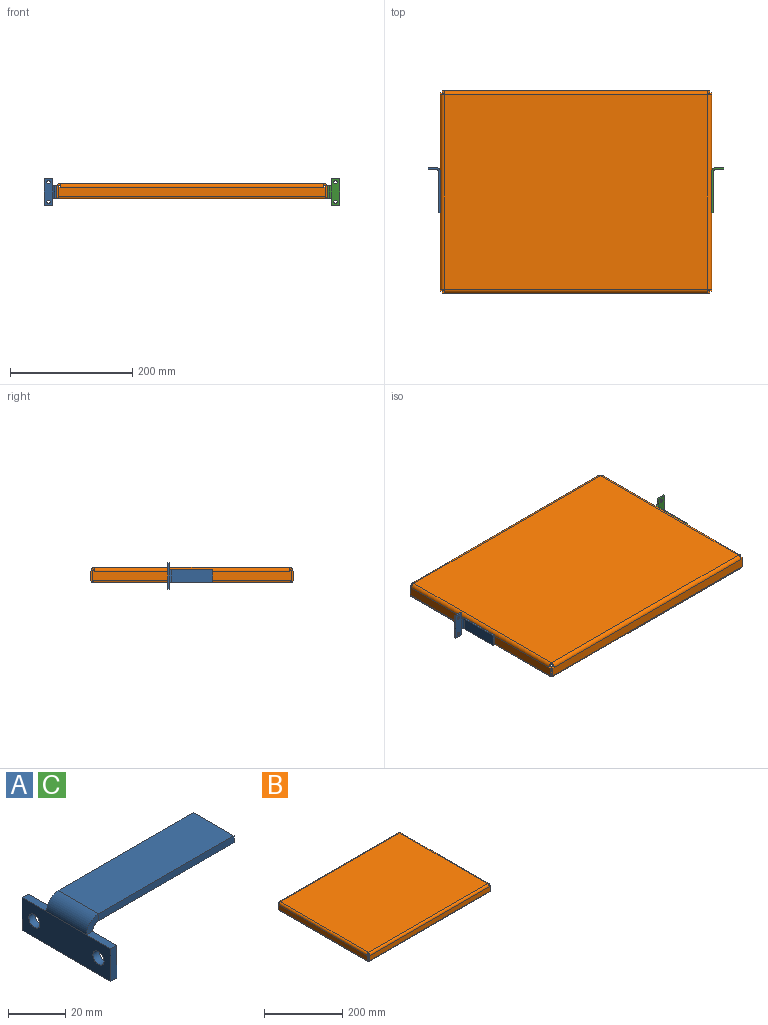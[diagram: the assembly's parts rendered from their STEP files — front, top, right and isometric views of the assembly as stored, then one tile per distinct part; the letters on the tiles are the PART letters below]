
ASSEMBLY  parts=3 mates=6
PART A: 18 faces, bbox 73x44x20 mm
  f0: plane 67x3mm, normal (0,1,0), area 201mm2, adj f2,f3,f4,f15
  f1: plane 67x3mm, normal (0,-1,0), area 201mm2, adj f2,f3,f4,f14
  f2: plane 20x3mm, normal (1,0,0), area 60mm2, adj f0,f1,f3,f4
  f3: plane 67x20mm, normal (0,0,1), area 1340mm2, adj f0,f1,f2,f16
  f4: plane 67x20mm, normal (0,0,-1), area 1340mm2, adj f0,f1,f2,f17
  f5: plane 12x3mm, normal (0,0,1), area 36mm2, adj f6,f12,f13,f15
  f6: plane 14x3mm, normal (0,1,0), area 42mm2, adj f5,f7,f12,f13
  f7: plane 44x3mm, normal (0,0,-1), area 132mm2, adj f6,f8,f12,f13
  f8: plane 14x3mm, normal (0,-1,0), area 42mm2, adj f7,f9,f12,f13
  f9: plane 12x3mm, normal (0,0,1), area 36mm2, adj f8,f12,f13,f14
  f10: cylinder r=2.75mm len=5.5mm, axis (-1,0,0), area 51.8mm2, adj f12,f13
  f11: cylinder r=2.75mm len=5.5mm, axis (-1,0,0), area 51.8mm2, adj f12,f13
  f12: plane 44x14mm, normal (-1,0,0), area 568.5mm2, adj f5,f6,f7,f8,f9,f10,f11,f16
  f13: plane 44x14mm, normal (1,0,0), area 568.5mm2, adj f5,f6,f7,f8,f9,f10,f11,f17
  f14: plane 6x6mm, normal (0,-1,0), area 21.2mm2, adj f1,f9,f16,f17
  f15: plane 6x6mm, normal (0,1,0), area 21.2mm2, adj f0,f5,f16,f17
  f16: cylinder r=6mm len=20mm, axis (0,-1,0), area 188.5mm2, adj f3,f12,f14,f15
  f17: cylinder r=3mm len=20mm, axis (0,-1,0), area 94.2mm2, adj f4,f13,f14,f15
PART B: 78 faces, bbox 443x330x25 mm
  f0: plane 431x318mm, normal (0,0,1), area 137058mm2, adj f19,f29,f57,f67
  f1: plane 431x318mm, normal (0,0,-1), area 137058mm2, adj f20,f30,f58,f68
  f2: plane 3x2.98mm, normal (0,0,1), area 8.9mm2, adj f3,f6,f7,f18
  f3: plane 15.99x3mm, normal (1,0,0), area 48mm2, adj f2,f6,f7,f9
  f4: plane 3x2.98mm, normal (0,0,1), area 8.9mm2, adj f5,f6,f7,f17
  f5: plane 15.99x3mm, normal (-1,0,0), area 48mm2, adj f4,f6,f7,f8
  f6: plane 436.96x15.99mm, normal (0,-1,0), area 6987mm2, adj f2,f3,f4,f5,f10,f19
  f7: plane 436.96x15.99mm, normal (0,1,0), area 6987mm2, adj f2,f3,f4,f5,f11,f20
  f8: bspline ~6.02x3.19mm, area 17.9mm2, adj f5,f10,f11,f12
  f9: bspline ~6.02x3.19mm, area 17.9mm2, adj f3,f10,f11,f14
  f10: cylinder r=3.01mm len=436.96mm, axis (1,0,0), area 4101.8mm2, adj f6,f8,f9,f15
  f11: cylinder r=0.01mm len=436.96mm, axis (1,0,0), area 13.6mm2, adj f7,f8,f9,f16
  f12: plane 14.99x3mm, normal (-1,0,0), area 45mm2, adj f8,f13,f15,f16
  f13: plane 430.59x3mm, normal (0,0,1), area 1291.8mm2, adj f12,f14,f15,f16
  f14: plane 14.99x3mm, normal (1,0,0), area 45mm2, adj f9,f13,f15,f16
  f15: plane 430.59x14.99mm, normal (0,1,0), area 6454.5mm2, adj f10,f12,f13,f14
  f16: plane 430.59x14.99mm, normal (0,-1,0), area 6454.5mm2, adj f11,f12,f13,f14
  f17: plane 6x6mm, normal (-1,0,0), area 21.2mm2, adj f4,f19,f20,f66
  f18: plane 6x6mm, normal (1,0,0), area 21.2mm2, adj f2,f19,f20,f56
  f19: cylinder r=6mm len=431mm, axis (-1,0,0), area 4062.1mm2, adj f0,f6,f17,f18
  f20: cylinder r=3mm len=431mm, axis (-1,0,0), area 2031mm2, adj f1,f7,f17,f18
  f21: plane 3x2.98mm, normal (0,0,1), area 8.9mm2, adj f22,f25,f26,f27
  f22: plane 15.99x3mm, normal (-1,0,0), area 48mm2, adj f21,f25,f26,f32
  f23: plane 3x2.98mm, normal (0,0,1), area 8.9mm2, adj f24,f25,f26,f28
  f24: plane 15.99x3mm, normal (1,0,0), area 48mm2, adj f23,f25,f26,f31
  f25: plane 436.96x15.99mm, normal (0,1,0), area 6987mm2, adj f21,f22,f23,f24,f29,f33
  f26: plane 436.96x15.99mm, normal (0,-1,0), area 6987mm2, adj f21,f22,f23,f24,f30,f34
  f27: plane 6x6mm, normal (-1,0,0), area 21.2mm2, adj f21,f29,f30,f65
  f28: plane 6x6mm, normal (1,0,0), area 21.2mm2, adj f23,f29,f30,f55
  f29: cylinder r=6mm len=431mm, axis (-1,0,0), area 4062.1mm2, adj f0,f25,f27,f28
  f30: cylinder r=3mm len=431mm, axis (-1,0,0), area 2031mm2, adj f1,f26,f27,f28
  f31: bspline ~6.02x3.19mm, area 17.9mm2, adj f24,f33,f34,f35
  f32: bspline ~6.02x3.19mm, area 17.9mm2, adj f22,f33,f34,f37
  f33: cylinder r=3.01mm len=436.96mm, axis (-1,0,0), area 4101.8mm2, adj f25,f31,f32,f38
  f34: cylinder r=0.01mm len=436.96mm, axis (-1,0,0), area 13.6mm2, adj f26,f31,f32,f39
  f35: plane 14.99x3mm, normal (1,0,0), area 45mm2, adj f31,f36,f38,f39
  f36: plane 430.59x3mm, normal (0,0,1), area 1291.8mm2, adj f35,f37,f38,f39
  f37: plane 14.99x3mm, normal (-1,0,0), area 45mm2, adj f32,f36,f38,f39
  f38: plane 430.59x14.99mm, normal (0,-1,0), area 6454.5mm2, adj f33,f35,f36,f37
  f39: plane 430.59x14.99mm, normal (0,1,0), area 6454.5mm2, adj f34,f35,f36,f37
  f40: plane 3x2.98mm, normal (0,0,1), area 8.9mm2, adj f41,f44,f45,f55
  f41: plane 15.99x3mm, normal (0,1,0), area 48mm2, adj f40,f44,f45,f47
  f42: plane 3x2.98mm, normal (0,0,1), area 8.9mm2, adj f43,f44,f45,f56
  f43: plane 15.99x3mm, normal (0,-1,0), area 48mm2, adj f42,f44,f45,f46
  f44: plane 323.96x15.99mm, normal (1,0,0), area 5180.1mm2, adj f40,f41,f42,f43,f48,f57
  f45: plane 323.96x15.99mm, normal (-1,0,0), area 5180.1mm2, adj f40,f41,f42,f43,f49,f58
  f46: bspline ~6.02x3.19mm, area 17.9mm2, adj f43,f48,f49,f50
  f47: bspline ~6.02x3.19mm, area 17.9mm2, adj f41,f48,f49,f52
  f48: cylinder r=3.01mm len=323.96mm, axis (0,1,0), area 3033.3mm2, adj f44,f46,f47,f53
  f49: cylinder r=0.01mm len=323.96mm, axis (0,1,0), area 10.1mm2, adj f45,f46,f47,f54
  f50: plane 14.99x3mm, normal (0,-1,0), area 45mm2, adj f46,f51,f53,f54
  f51: plane 317.59x3mm, normal (0,0,1), area 952.8mm2, adj f50,f52,f53,f54
  f52: plane 14.99x3mm, normal (0,1,0), area 45mm2, adj f47,f51,f53,f54
  f53: plane 317.59x14.99mm, normal (-1,0,0), area 4760.6mm2, adj f48,f50,f51,f52
  f54: plane 317.59x14.99mm, normal (1,0,0), area 4760.6mm2, adj f49,f50,f51,f52
  f55: plane 6x6mm, normal (0,1,0), area 21.2mm2, adj f28,f40,f57,f58
  f56: plane 6x6mm, normal (0,-1,0), area 21.2mm2, adj f18,f42,f57,f58
  f57: cylinder r=6mm len=318mm, axis (0,1,0), area 2997.1mm2, adj f0,f44,f55,f56
  f58: cylinder r=3mm len=318mm, axis (0,1,0), area 1498.5mm2, adj f1,f45,f55,f56
  f59: plane 3x2.98mm, normal (0,0,1), area 8.9mm2, adj f60,f63,f64,f66
  f60: plane 15.99x3mm, normal (0,-1,0), area 48mm2, adj f59,f63,f64,f70
  f61: plane 3x2.98mm, normal (0,0,1), area 8.9mm2, adj f62,f63,f64,f65
  f62: plane 15.99x3mm, normal (0,1,0), area 48mm2, adj f61,f63,f64,f69
  f63: plane 323.96x15.99mm, normal (-1,0,0), area 5180.1mm2, adj f59,f60,f61,f62,f67,f71
  f64: plane 323.96x15.99mm, normal (1,0,0), area 5180.1mm2, adj f59,f60,f61,f62,f68,f72
  f65: plane 6x6mm, normal (0,1,0), area 21.2mm2, adj f27,f61,f67,f68
  f66: plane 6x6mm, normal (0,-1,0), area 21.2mm2, adj f17,f59,f67,f68
  f67: cylinder r=6mm len=318mm, axis (0,1,0), area 2997.1mm2, adj f0,f63,f65,f66
  f68: cylinder r=3mm len=318mm, axis (0,1,0), area 1498.5mm2, adj f1,f64,f65,f66
  f69: bspline ~6.02x3.19mm, area 17.9mm2, adj f62,f71,f72,f73
  f70: bspline ~6.02x3.19mm, area 17.9mm2, adj f60,f71,f72,f75
  f71: cylinder r=3.01mm len=323.96mm, axis (0,-1,0), area 3033.3mm2, adj f63,f69,f70,f76
  f72: cylinder r=0.01mm len=323.96mm, axis (0,-1,0), area 10.1mm2, adj f64,f69,f70,f77
  f73: plane 14.99x3mm, normal (0,1,0), area 45mm2, adj f69,f74,f76,f77
  f74: plane 317.59x3mm, normal (0,0,1), area 952.8mm2, adj f73,f75,f76,f77
  f75: plane 14.99x3mm, normal (0,-1,0), area 45mm2, adj f70,f74,f76,f77
  f76: plane 317.59x14.99mm, normal (1,0,0), area 4760.6mm2, adj f71,f73,f74,f75
  f77: plane 317.59x14.99mm, normal (-1,0,0), area 4760.6mm2, adj f72,f73,f74,f75
PART C: same geometry as A
PLACE A rot(axis=(-0.58,0.58,-0.58),120deg) t=(18.49,42.86,-1.71)mm
PLACE B t=(239.99,41.36,12.29)mm
PLACE C rot(axis=(0.58,-0.58,-0.58),120deg) t=(461.49,42.86,-1.71)mm
MATE parallel C.f0 <-> B.f0  axis (0,0,1) through (462.99,41.36,8.29)mm
MATE parallel A.f1 <-> B.f0  axis (0,0,1) through (16.99,41.36,8.29)mm
MATE slider C.f3 <-> B.f44  axis (-1,0,0) through (461.49,41.36,-1.71)mm
MATE slider A.f3 <-> B.f63  axis (1,0,0) through (18.49,41.36,-1.71)mm
MATE planar C.f3 <-> B.f44  axis (-1,0,0) through (461.49,41.36,-1.71)mm
MATE planar A.f3 <-> B.f63  axis (1,0,0) through (18.49,41.36,-1.71)mm
